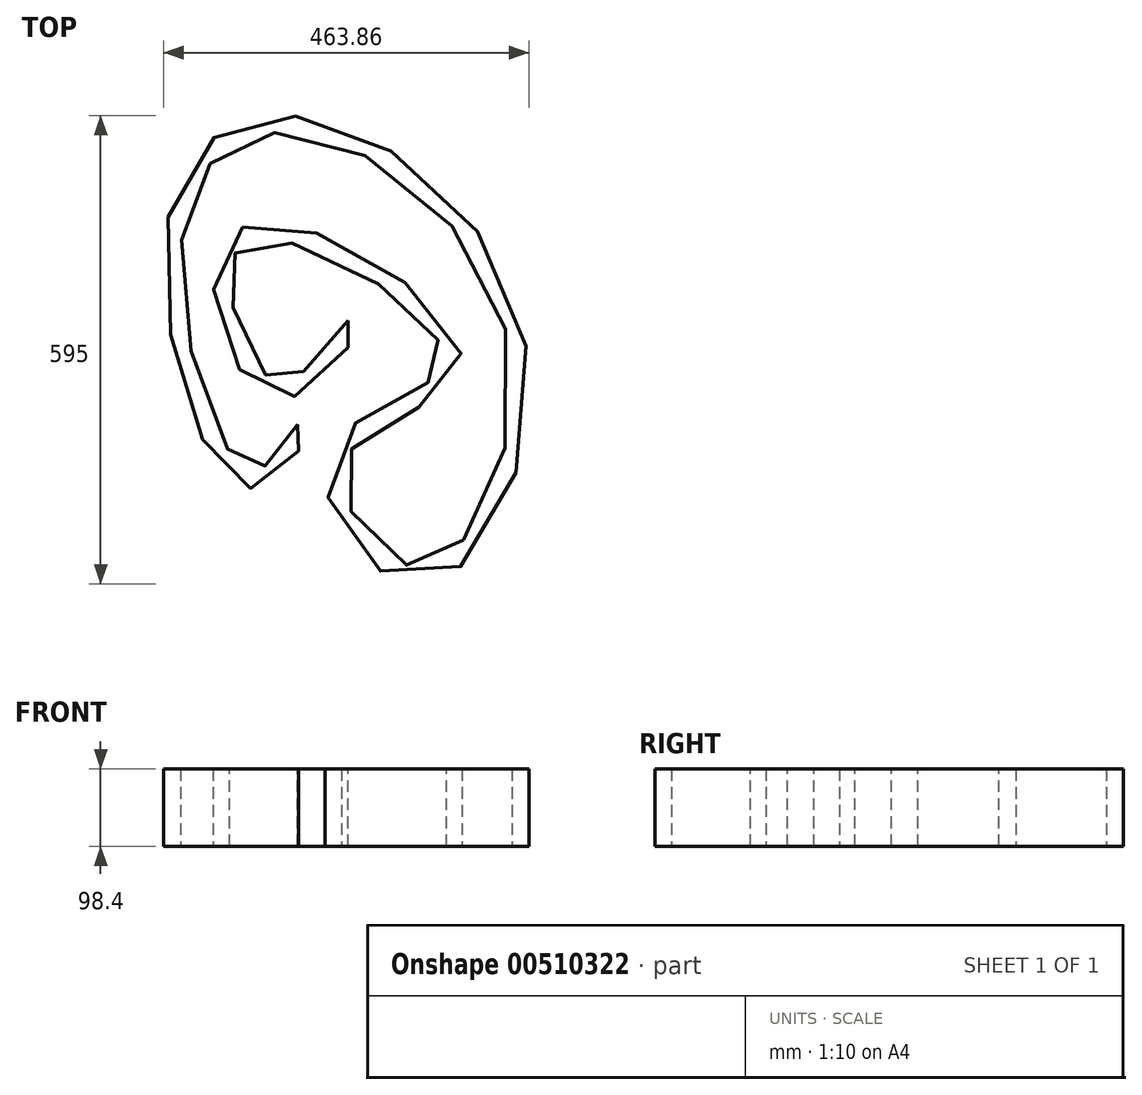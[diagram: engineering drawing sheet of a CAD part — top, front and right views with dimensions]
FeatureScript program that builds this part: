
annotation { "Feature Type Name" : "Feature", "Feature Type Description" : "" }
export const myFeature = defineFeature(function(context is Context, id is Id, definition is map)
    precondition{}
    {
        {
            var Q0;
            Q0=qCreatedBy(makeId("Right.planeOp"),FACE);
            var sketch = newSketch(context, id + "F0", { "sketchPlane" : qUnion([Q0])});
            skLineSegment(sketch, "E0.bottom", {"start": v(-16.9, -49.2) * mm, "end": v(16.9, -49.2) * mm});
            skLineSegment(sketch, "E0.top", {"start": v(-16.9, 49.2) * mm, "end": v(16.9, 49.2) * mm});
            skLineSegment(sketch, "E0.left", {"start": v(-16.9, -49.2) * mm, "end": v(-16.9, 49.2) * mm});
            skLineSegment(sketch, "E0.right", {"start": v(16.9, -49.2) * mm, "end": v(16.9, 49.2) * mm});
            skPoint(sketch, "E0.middle", {"position": v(0, 0) * mm});
            skSolve(sketch);
        }
        {
            var Q0;
            Q0=qCreatedBy(makeId("Top.planeOp"),FACE);
            var sketch = newSketch(context, id + "F1", { "sketchPlane" : qUnion([Q0])});
            skFitSpline(sketch, "E1", {"points": [v(0, 0) * mm, v(-98.73, -67.85) * mm, v(-156.75, 93.11) * mm, v(-43.52, 117.91) * mm, v(131.01, -43.05) * mm, v(-13.1, -156.75) * mm, v(88.9, -305.54) * mm, v(213.37, -4.68) * mm, v(-69.25, 265.77) * mm, v(-219.45, 138.03) * mm, v(-133.82, -180.61) * mm, v(-63.17, -131.95) * mm], "startDerivative": vector(-1442.59, -1762.4) * mm, "endDerivative": vector(1162.66, 1525.1) * mm});
            skSolve(sketch);
        }
        {
            var Q0;
            Q0=makeQuery(id+"F0.imprint","IMPRINT",FACE,{"disambiguationData":[TD([[makeQuery(id+"F0.imprint","IMPRINT",EDGE,{"derivedFrom":sQuery(id+"F0.wireOp",EDGE,"E0.bottom")}),1.0]])]});
            var Q1;
            Q1=sQuery(id+"F1.wireOp",EDGE,"E1");
            sweep(context, id + "F2", {"profiles" : qUnion([Q0]), "path" : qUnion([Q1])});
        }
    });
